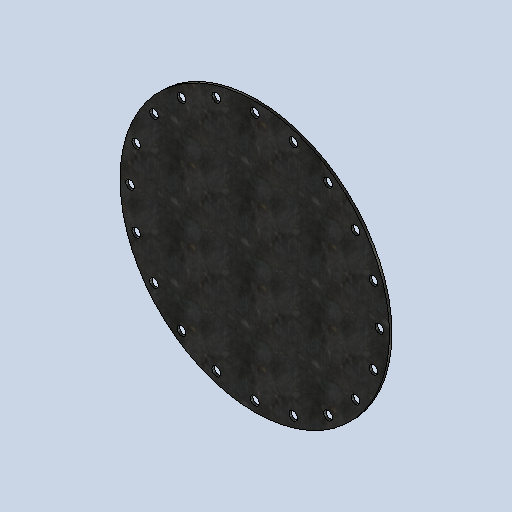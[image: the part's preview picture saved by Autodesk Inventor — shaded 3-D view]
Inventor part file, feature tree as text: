
AUTODESK INVENTOR PART (.ipt)
format: ipt  version: 2025.1 (Build 291241020, 241B)  size: 256,000 bytes
history: native  units: mm
features: sketch x2, other x2, extrude x1, pattern_circular x1
ambient origin geometry x8: Origin, YZ Plane, XZ Plane, XY Plane, X Axis, Y Axis, Z Axis, Center Point
bodies: Solid1 (feature_tree)
feature tree (6):
  extrude  "Extrusion1"  Depth=6.0mm TaperAngle=0.0deg
  pattern_circular  "Circular Pattern1"  Count=62  [1 undecoded]
  sketch  "Sketch1"  dims[d0=670.0mm d1=6.0mm d2=0.0mm]
  sketch  "Sketch2"  dims[d3=22.0mm d4=620.0mm d5=6.0mm d6=6.0mm d7=0.0mm d8=200.0mm d9=360.0deg]
  other  "Cut1"
  other  "Definition1"
note: 1 required parameter value undecoded (feature->parameter linkage not recoverable at this tier; creation-order binding heuristic only, values carry confidence <= 0.55)
